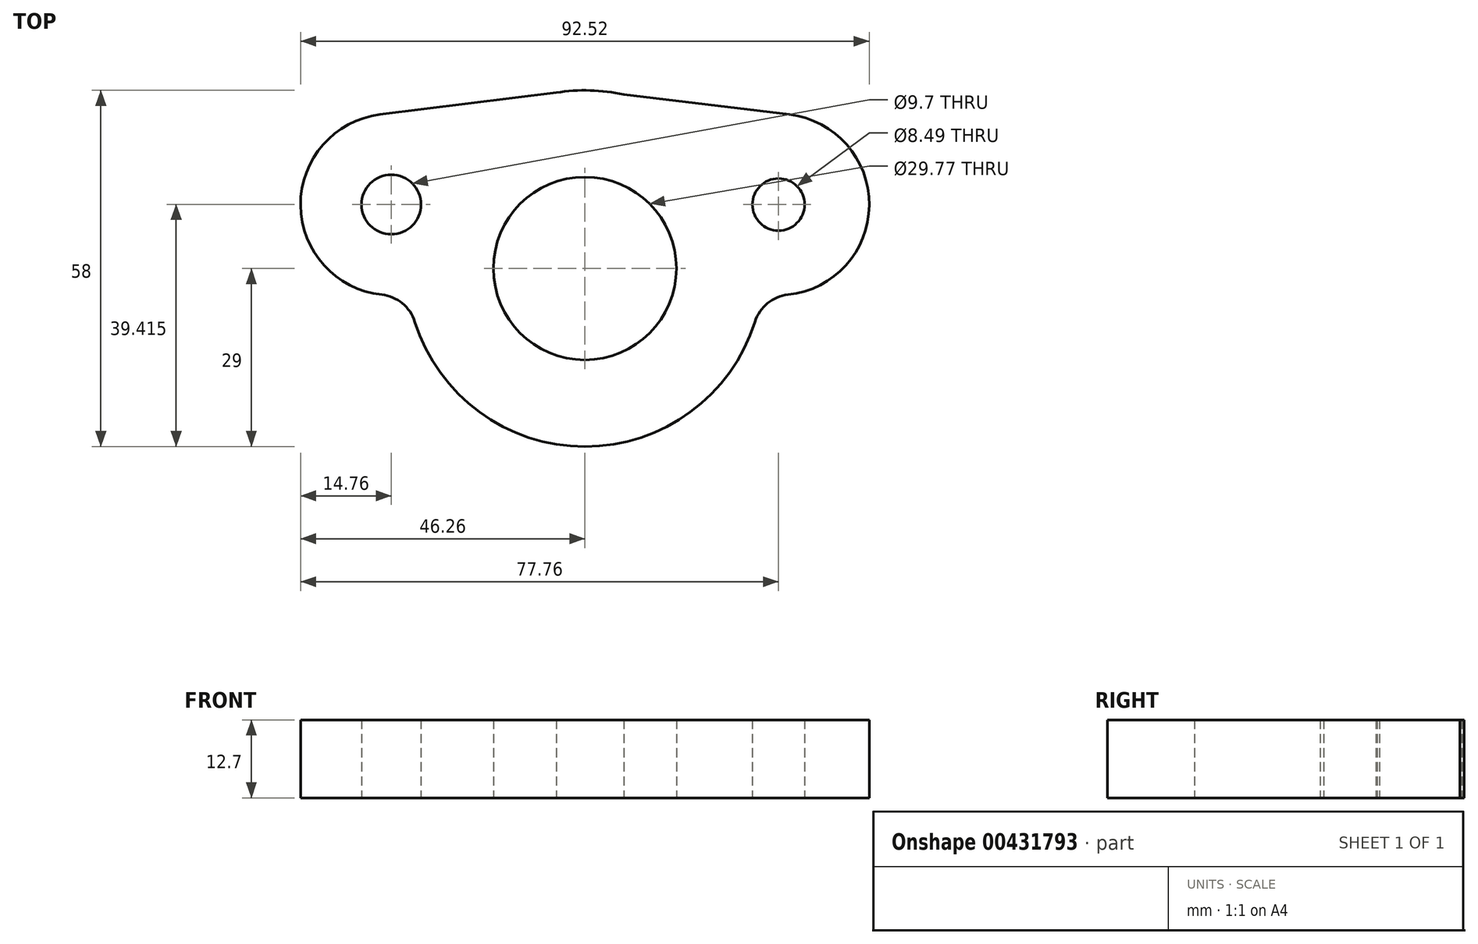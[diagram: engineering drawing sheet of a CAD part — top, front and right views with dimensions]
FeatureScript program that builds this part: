
annotation { "Feature Type Name" : "Feature", "Feature Type Description" : "" }
export const myFeature = defineFeature(function(context is Context, id is Id, definition is map)
    precondition{}
    {
        {
            var Q0;
            Q0=qCreatedBy(makeId("Top.planeOp"),FACE);
            var sketch = newSketch(context, id + "F0", { "sketchPlane" : qUnion([Q0])});
            skCircle(sketch, "E0", {"center": v(0, 0) * mm, "radius": 18.41 * mm});
            skCircle(sketch, "E1", {"center": v(-31.5, 10.41) * mm, "radius": 4.85 * mm});
            skCircle(sketch, "E2", {"center": v(31.5, 10.42) * mm, "radius": 4.24 * mm});
            skArc(sketch, "E3", {"start": v(-33.32, 25.06) * mm, "mid": v(-46.26, 10.28) * mm, "end": v(-33.06, -4.26) * mm});
            skArc(sketch, "E4", {"start": v(33.06, -4.26) * mm, "mid": v(46.26, 10.32) * mm, "end": v(33.26, 25.07) * mm});
            skArc(sketch, "E5.trimOffspring", {"start": v(-27.67, -8.68) * mm, "mid": v(0, -29) * mm, "end": v(27.67, -8.68) * mm});
            skArc(sketch, "E6.trimOffspring", {"start": v(6.32, 28.3) * mm, "mid": v(0.85, 28.99) * mm, "end": v(-4.65, 28.62) * mm});
            skLineSegment(sketch, "E7", {"start": v(-33.32, 25.06) * mm, "end": v(-4.65, 28.62) * mm});
            skLineSegment(sketch, "E8", {"start": v(6.32, 28.3) * mm, "end": v(33.26, 25.07) * mm});
            skPoint(sketch, "E9.visualSharp", {"position": v(-28.71, -4.08) * mm});
            skArc(sketch, "E9.filletArc", {"start": v(-27.67, -8.68) * mm, "mid": v(-29.7, -5.67) * mm, "end": v(-33.06, -4.26) * mm});
            skPoint(sketch, "E10.visualSharp", {"position": v(28.71, -4.08) * mm});
            skArc(sketch, "E10.filletArc", {"start": v(33.06, -4.26) * mm, "mid": v(29.7, -5.67) * mm, "end": v(27.67, -8.68) * mm});
            skSolve(sketch);
        }
        {
            var Q0;
            Q0=makeQuery(id+"F0.imprint","IMPRINT",FACE,{"disambiguationData":[TD([[makeQuery(id+"F0.imprint","IMPRINT",EDGE,{"derivedFrom":sQuery(id+"F0.wireOp",EDGE,"E0")}),-1.0]])]});
            var Q1;
            Q1=makeQuery(id+"F0.imprint","IMPRINT",FACE,{"disambiguationData":[TD([[makeQuery(id+"F0.imprint","IMPRINT",EDGE,{"derivedFrom":sQuery(id+"F0.wireOp",EDGE,"E0")}),1.0]])]});
            extrude(context, id + "F1", {"entities" : qUnion([Q0, Q1]), "depth" : 12.7 * mm});
        }
        {
            var Q0;
            Q0=qCreatedBy(makeId("Top.planeOp"),FACE);
            var sketch = newSketch(context, id + "F2", { "sketchPlane" : qUnion([Q0])});
            skPoint(sketch, "E11", {"position": v(0, 0) * mm});
            skSolve(sketch);
        }
        {
            var Q0;
            Q0=sQuery(id+"F2.wireOp",VERTEX,"E11");
            var Q1;
            Q1=makeQuery(id+"F1.opExtrude","SWEPT_BODY",BODY,{"disambiguationData":[OSD([sQuery(id+"F0.wireOp",EDGE,"E1"),sQuery(id+"F0.wireOp",EDGE,"E2"),sQuery(id+"F0.wireOp",EDGE,"E3"),sQuery(id+"F0.wireOp",EDGE,"E4"),sQuery(id+"F0.wireOp",EDGE,"E5.trimOffspring"),sQuery(id+"F0.wireOp",EDGE,"E6.trimOffspring"),sQuery(id+"F0.wireOp",EDGE,"E7"),sQuery(id+"F0.wireOp",EDGE,"E8"),sQuery(id+"F0.wireOp",EDGE,"E9.filletArc"),sQuery(id+"F0.wireOp",EDGE,"E10.filletArc")])]});
            hole(context, id + "F3", {"style" : HoleStyle.SIMPLE, "endStyle" : HoleEndStyle.THROUGH, "oppositeDirection" : true, "standardTappedOrClearance" : lookupTablePath({ "standard" : "ANSI", "engagement" : "75%", "pitch" : "12 tpi", "size" : "1 1/4", "type" : "Tapped" }), "standardBlindInLast" : lookupTablePath({ "standard" : "ANSI", "engagement" : "75%", "pitch" : "12 tpi", "size" : "1 1/4", "type" : "Tapped" }), "holeDiameter" : 29.77 * mm, "showTappedDepth" : true, "isTappedThrough" : true, "tappedDepth" : 12.7 * mm, "tapClearance" : 3, "locations" : qUnion([Q0]), "scope" : qUnion([Q1]), "majorDiameter" : 31.75 * mm});
        }
    });
